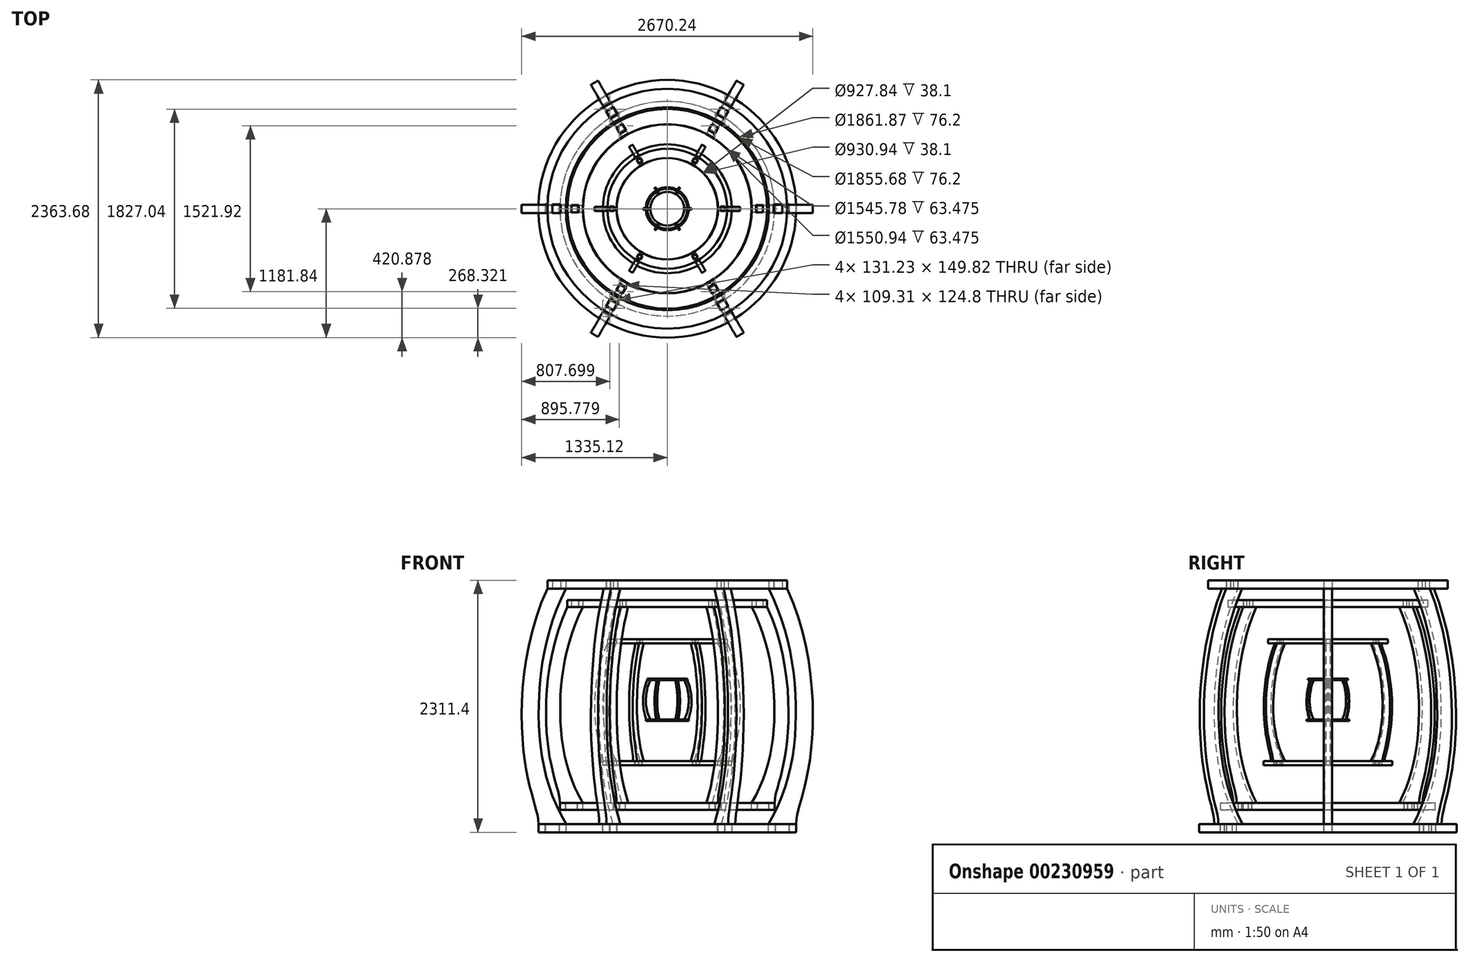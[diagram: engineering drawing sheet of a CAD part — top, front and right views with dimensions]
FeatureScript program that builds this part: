
annotation { "Feature Type Name" : "Feature", "Feature Type Description" : "" }
export const myFeature = defineFeature(function(context is Context, id is Id, definition is map)
    precondition{}
    {
        {
            var Q0;
            Q0=qCreatedBy(makeId("Front.planeOp"),FACE);
            var sketch = newSketch(context, id + "F0", { "sketchPlane" : qUnion([Q0])});
            skLineSegment(sketch, "E0", {"start": v(-1181.84, -1150.9) * mm, "end": v(-927.84, -1150.9) * mm});
            skFitSpline(sketch, "E1", {"points": [v(0, 1953.34) * mm, v(-1100.72, 1005.82) * mm, v(-1321.31, -446.03) * mm, v(-1216.83, -971.67) * mm, v(-1181.84, -1150.9) * mm], "startDerivative": vector(-4000.43, 5.06) * mm, "endDerivative": vector(0, -1489.55) * mm});
            skLineSegment(sketch, "E2", {"start": v(-1099.69, 1008.1) * mm, "end": v(-930.94, 1008.1) * mm});
            skLineSegment(sketch, "E3", {"start": v(-1181.84, -1150.9) * mm, "end": v(-1181.84, -1354.1) * mm});
            skLineSegment(sketch, "E4", {"start": v(-1181.84, -1354.1) * mm, "end": v(-877.04, -1354.1) * mm});
            skLineSegment(sketch, "E5", {"start": v(-877.04, -1354.1) * mm, "end": v(-877.04, -1252.5) * mm});
            skLineSegment(sketch, "E6", {"start": v(-877.04, -1252.5) * mm, "end": v(-927.84, -1252.5) * mm});
            skLineSegment(sketch, "E7", {"start": v(-927.84, -1252.5) * mm, "end": v(-927.84, -1150.9) * mm});
            skFitSpline(sketch, "E8.trimOffspring", {"points": [v(0, -1757.92) * mm, v(-927.84, -1150.9) * mm, v(-1179.31, -127.8) * mm, v(-917.89, 1034.08) * mm, v(0, 1800.66) * mm], "startDerivative": vector(-4973.2, 113.59) * mm, "endDerivative": vector(4756.7, 336.76) * mm});
            skLineSegment(sketch, "E9", {"start": v(-1023.33, 1160.5) * mm, "end": v(-848.12, 1160.5) * mm});
            skLineSegment(sketch, "E10", {"start": v(0, 1953.34) * mm, "end": v(0, 1800.66) * mm});
            skLineSegment(sketch, "E11.bottom", {"start": v(-1118.34, -1074.7) * mm, "end": v(-991.34, -1074.7) * mm});
            skLineSegment(sketch, "E11.top", {"start": v(-1118.34, -1227.1) * mm, "end": v(-991.34, -1227.1) * mm});
            skLineSegment(sketch, "E11.left", {"start": v(-1118.34, -1074.7) * mm, "end": v(-1118.34, -1227.1) * mm});
            skLineSegment(sketch, "E11.right", {"start": v(-991.34, -1074.7) * mm, "end": v(-991.34, -1227.1) * mm});
            skPoint(sketch, "E11.middle", {"position": v(-1054.84, -1150.9) * mm});
            skLineSegment(sketch, "E12.bottom", {"start": v(-1053.41, 1084.3) * mm, "end": v(-977.21, 1084.3) * mm});
            skLineSegment(sketch, "E12.top", {"start": v(-1053.41, 931.9) * mm, "end": v(-977.21, 931.9) * mm});
            skLineSegment(sketch, "E12.left", {"start": v(-1053.41, 1084.3) * mm, "end": v(-1053.41, 931.9) * mm});
            skLineSegment(sketch, "E12.right", {"start": v(-977.21, 1084.3) * mm, "end": v(-977.21, 931.9) * mm});
            skPoint(sketch, "E12.middle", {"position": v(-1015.31, 1008.1) * mm});
            skSolve(sketch);
        }
        {
            var Q0;
            {var subQ5=sQuery(id+"F0.wireOp",EDGE,"E12.bottom");Q0=makeQuery(id+"F0.imprint","IMPRINT",FACE,{"disambiguationData":[TD([[makeQuery(id+"F0.imprint","IMPRINT",EDGE,{"derivedFrom":subQ5}),-1.0]])]});}
            var Q1;
            {var subQ5=sQuery(id+"F0.wireOp",EDGE,"E11.top");Q1=makeQuery(id+"F0.imprint","IMPRINT",FACE,{"disambiguationData":[TD([[makeQuery(id+"F0.imprint","IMPRINT",EDGE,{"derivedFrom":subQ5}),1.0]])]});}
            var Q2;
            {var subQ0=sQuery(id+"F0.wireOp",EDGE,"E11.left");var subQ3=sQuery(id+"F0.wireOp",EDGE,"E0");var subQ4=makeQuery(id+"F0.imprint","INTERSECT",VERTEX,{"derivedFrom":[subQ3,subQ0]});Q2=makeQuery(id+"F0.imprint","IMPRINT",FACE,{"disambiguationData":[TD([[makeQuery(id+"F0.imprint","IMPRINT",EDGE,{"disambiguationData":[TD([[subQ4,-1.0]])],"derivedFrom":subQ3}),1.0]])]});}
            var Q3;
            {var subQ0=sQuery(id+"F0.wireOp",EDGE,"E2");var subQ1=sQuery(id+"F0.wireOp",EDGE,"E1");var subQ2=makeQuery(id+"F0.imprint","INTERSECT",VERTEX,{"derivedFrom":[subQ1,subQ0]});Q3=makeQuery(id+"F0.imprint","IMPRINT",FACE,{"disambiguationData":[TD([[makeQuery(id+"F0.imprint","IMPRINT",EDGE,{"disambiguationData":[TD([[subQ2,-1.0]])],"derivedFrom":subQ0}),-1.0]])]});}
            var Q4;
            {var subQ0=sQuery(id+"F0.wireOp",EDGE,"E8.trimOffspring");var subQ1=sQuery(id+"F0.wireOp",EDGE,"E2");var subQ2=makeQuery(id+"F0.imprint","INTERSECT",VERTEX,{"derivedFrom":[subQ1,subQ0]});Q4=makeQuery(id+"F0.imprint","IMPRINT",FACE,{"disambiguationData":[TD([[makeQuery(id+"F0.imprint","IMPRINT",EDGE,{"disambiguationData":[TD([[subQ2,1.0]])],"derivedFrom":subQ1}),-1.0]])]});}
            var Q5;
            {var subQ0=sQuery(id+"F0.wireOp",EDGE,"E12.left");var subQ5=sQuery(id+"F0.wireOp",EDGE,"E2");var subQ6=makeQuery(id+"F0.imprint","INTERSECT",VERTEX,{"derivedFrom":[subQ5,subQ0]});Q5=makeQuery(id+"F0.imprint","IMPRINT",FACE,{"disambiguationData":[TD([[makeQuery(id+"F0.imprint","IMPRINT",EDGE,{"disambiguationData":[TD([[subQ6,-1.0]])],"derivedFrom":subQ5}),-1.0]])]});}
            extrude(context, id + "F1", {"entities" : qUnion([Q0, Q1, Q2, Q3, Q4, Q5]), "endBound" : BoundingType.SYMMETRIC, "depth" : 76.2 * mm});
        }
        {
            var Q0;
            Q0=makeQuery(id+"F1.opExtrude","SWEPT_BODY",BODY,{"disambiguationData":[OSD([sQuery(id+"F0.wireOp",EDGE,"E0"),sQuery(id+"F0.wireOp",EDGE,"E1"),sQuery(id+"F0.wireOp",EDGE,"E2"),sQuery(id+"F0.wireOp",EDGE,"E8.trimOffspring")])]});
            var Q1;
            Q1=sQuery(id+"F0.wireOp",EDGE,"E10");
            circularPattern(context, id + "F2", {"entities" : qUnion([Q0]), "axis" : qUnion([Q1]), "angle" : 360 * degree, "instanceCount" : 6, "equalSpace" : true});
        }
        {
            var Q0;
            Q0=qCreatedBy(makeId("Top.planeOp"),FACE);
            var Q1;
            Q1=sQuery(id+"F0.wireOp",VERTEX,"E8.trimOffspring.1.internal");
            cPlane(context, id + "F3", {"entities" : qUnion([Q0, Q1]), "cplaneType" : CPlaneType.PLANE_POINT, "offset" : 25.4 * mm, "width" : 152.4 * mm, "height" : 152.4 * mm});
        }
        {
            var Q0;
            Q0=qCreatedBy(id+"F3.planeOp",FACE);
            var sketch = newSketch(context, id + "F4", { "sketchPlane" : qUnion([Q0])});
            skCircle(sketch, "E13", {"center": v(0, 0) * mm, "radius": 1181.84 * mm});
            skCircle(sketch, "E14", {"center": v(0, 0) * mm, "radius": 927.84 * mm});
            skLineSegment(sketch, "E15.bottom", {"start": v(-1118.98, 38.73) * mm, "end": v(-990.7, 38.73) * mm});
            skLineSegment(sketch, "E15.top", {"start": v(-1118.98, -38.74) * mm, "end": v(-990.7, -38.74) * mm});
            skLineSegment(sketch, "E15.left", {"start": v(-1118.98, 38.73) * mm, "end": v(-1118.98, -38.74) * mm});
            skLineSegment(sketch, "E15.right", {"start": v(-990.7, 38.73) * mm, "end": v(-990.7, -38.74) * mm});
            skPoint(sketch, "E15.middle", {"position": v(-1054.84, 0) * mm});
            skLineSegment(sketch, "E16.1.0", {"start": v(-593.03, -949.7) * mm, "end": v(-528.9, -838.6) * mm});
            skLineSegment(sketch, "E16.1.1", {"start": v(-593.03, -949.7) * mm, "end": v(-525.94, -988.43) * mm});
            skLineSegment(sketch, "E16.1.2", {"start": v(-525.94, -988.43) * mm, "end": v(-461.8, -877.34) * mm});
            skLineSegment(sketch, "E16.1.3", {"start": v(-528.9, -838.6) * mm, "end": v(-461.8, -877.34) * mm});
            skLineSegment(sketch, "E16.2.0", {"start": v(525.94, -988.43) * mm, "end": v(461.8, -877.34) * mm});
            skLineSegment(sketch, "E16.2.1", {"start": v(525.94, -988.43) * mm, "end": v(593.03, -949.7) * mm});
            skLineSegment(sketch, "E16.2.2", {"start": v(593.03, -949.7) * mm, "end": v(528.9, -838.6) * mm});
            skLineSegment(sketch, "E16.2.3", {"start": v(461.8, -877.34) * mm, "end": v(528.9, -838.6) * mm});
            skLineSegment(sketch, "E16.3.0", {"start": v(1118.98, -38.74) * mm, "end": v(990.7, -38.74) * mm});
            skLineSegment(sketch, "E16.3.1", {"start": v(1118.98, -38.74) * mm, "end": v(1118.98, 38.73) * mm});
            skLineSegment(sketch, "E16.3.2", {"start": v(1118.98, 38.73) * mm, "end": v(990.7, 38.73) * mm});
            skLineSegment(sketch, "E16.3.3", {"start": v(990.7, -38.74) * mm, "end": v(990.7, 38.73) * mm});
            skLineSegment(sketch, "E16.4.0", {"start": v(593.03, 949.7) * mm, "end": v(528.9, 838.6) * mm});
            skLineSegment(sketch, "E16.4.1", {"start": v(593.03, 949.7) * mm, "end": v(525.94, 988.43) * mm});
            skLineSegment(sketch, "E16.4.2", {"start": v(525.94, 988.43) * mm, "end": v(461.8, 877.34) * mm});
            skLineSegment(sketch, "E16.4.3", {"start": v(528.9, 838.6) * mm, "end": v(461.8, 877.34) * mm});
            skLineSegment(sketch, "E16.5.0", {"start": v(-525.94, 988.43) * mm, "end": v(-461.8, 877.34) * mm});
            skLineSegment(sketch, "E16.5.1", {"start": v(-525.94, 988.43) * mm, "end": v(-593.03, 949.7) * mm});
            skLineSegment(sketch, "E16.5.2", {"start": v(-593.03, 949.7) * mm, "end": v(-528.9, 838.6) * mm});
            skLineSegment(sketch, "E16.5.3", {"start": v(-461.8, 877.34) * mm, "end": v(-528.9, 838.6) * mm});
            skSolve(sketch);
        }
        {
            var Q0;
            Q0=makeQuery(id+"F4.imprint","IMPRINT",FACE,{"disambiguationData":[TD([[makeQuery(id+"F4.imprint","IMPRINT",EDGE,{"derivedFrom":sQuery(id+"F4.wireOp",EDGE,"E13")}),1.0]])]});
            extrude(context, id + "F5", {"entities" : qUnion([Q0]), "oppositeDirection" : true, "depth" : 76.2 * mm});
        }
        {
            var Q0;
            Q0=qCreatedBy(makeId("Top.planeOp"),FACE);
            var Q1;
            Q1=sQuery(id+"F0.wireOp",VERTEX,"E2.end");
            cPlane(context, id + "F6", {"entities" : qUnion([Q0, Q1]), "cplaneType" : CPlaneType.PLANE_POINT, "offset" : 25.4 * mm, "width" : 152.4 * mm, "height" : 152.4 * mm});
        }
        {
            var Q0;
            Q0=qCreatedBy(id+"F6.planeOp",FACE);
            var sketch = newSketch(context, id + "F7", { "sketchPlane" : qUnion([Q0])});
            skCircle(sketch, "E17", {"center": v(0, 0) * mm, "radius": 1099.69 * mm});
            skCircle(sketch, "E18", {"center": v(0, 0) * mm, "radius": 930.94 * mm});
            skLineSegment(sketch, "E19.bottom", {"start": v(-1054.05, 38.74) * mm, "end": v(-976.58, 38.74) * mm});
            skLineSegment(sketch, "E19.top", {"start": v(-1054.05, -38.73) * mm, "end": v(-976.58, -38.73) * mm});
            skLineSegment(sketch, "E19.left", {"start": v(-1054.05, 38.74) * mm, "end": v(-1054.05, -38.73) * mm});
            skLineSegment(sketch, "E19.right", {"start": v(-976.58, 38.74) * mm, "end": v(-976.58, -38.73) * mm});
            skPoint(sketch, "E19.middle", {"position": v(-1015.31, 0) * mm});
            skLineSegment(sketch, "E20.1.0", {"start": v(-560.57, -893.46) * mm, "end": v(-521.83, -826.37) * mm});
            skLineSegment(sketch, "E20.1.1", {"start": v(-560.57, -893.46) * mm, "end": v(-493.48, -932.2) * mm});
            skLineSegment(sketch, "E20.1.2", {"start": v(-493.48, -932.2) * mm, "end": v(-454.74, -865.1) * mm});
            skLineSegment(sketch, "E20.1.3", {"start": v(-521.83, -826.37) * mm, "end": v(-454.74, -865.1) * mm});
            skLineSegment(sketch, "E20.2.0", {"start": v(493.48, -932.2) * mm, "end": v(454.74, -865.1) * mm});
            skLineSegment(sketch, "E20.2.1", {"start": v(493.48, -932.2) * mm, "end": v(560.57, -893.46) * mm});
            skLineSegment(sketch, "E20.2.2", {"start": v(560.57, -893.46) * mm, "end": v(521.83, -826.37) * mm});
            skLineSegment(sketch, "E20.2.3", {"start": v(454.74, -865.1) * mm, "end": v(521.83, -826.37) * mm});
            skLineSegment(sketch, "E20.3.0", {"start": v(1054.05, -38.74) * mm, "end": v(976.58, -38.74) * mm});
            skLineSegment(sketch, "E20.3.1", {"start": v(1054.05, -38.74) * mm, "end": v(1054.05, 38.73) * mm});
            skLineSegment(sketch, "E20.3.2", {"start": v(1054.05, 38.73) * mm, "end": v(976.58, 38.73) * mm});
            skLineSegment(sketch, "E20.3.3", {"start": v(976.58, -38.74) * mm, "end": v(976.58, 38.73) * mm});
            skLineSegment(sketch, "E20.4.0", {"start": v(560.57, 893.46) * mm, "end": v(521.83, 826.37) * mm});
            skLineSegment(sketch, "E20.4.1", {"start": v(560.57, 893.46) * mm, "end": v(493.48, 932.2) * mm});
            skLineSegment(sketch, "E20.4.2", {"start": v(493.48, 932.2) * mm, "end": v(454.74, 865.1) * mm});
            skLineSegment(sketch, "E20.4.3", {"start": v(521.83, 826.37) * mm, "end": v(454.74, 865.1) * mm});
            skLineSegment(sketch, "E20.5.0", {"start": v(-493.48, 932.2) * mm, "end": v(-454.74, 865.1) * mm});
            skLineSegment(sketch, "E20.5.1", {"start": v(-493.48, 932.2) * mm, "end": v(-560.57, 893.46) * mm});
            skLineSegment(sketch, "E20.5.2", {"start": v(-560.57, 893.46) * mm, "end": v(-521.83, 826.37) * mm});
            skLineSegment(sketch, "E20.5.3", {"start": v(-454.74, 865.1) * mm, "end": v(-521.83, 826.37) * mm});
            skSolve(sketch);
        }
        {
            var Q0;
            Q0=makeQuery(id+"F7.imprint","IMPRINT",FACE,{"disambiguationData":[TD([[makeQuery(id+"F7.imprint","IMPRINT",EDGE,{"derivedFrom":sQuery(id+"F7.wireOp",EDGE,"E17")}),1.0]])]});
            extrude(context, id + "F8", {"entities" : qUnion([Q0]), "depth" : 76.2 * mm});
        }
        {
            var Q0;
            Q0=makeQuery(id+"F8.opExtrude","SWEPT_BODY",BODY,{"disambiguationData":[OSD([sQuery(id+"F7.wireOp",EDGE,"E17"),sQuery(id+"F7.wireOp",EDGE,"E18"),sQuery(id+"F7.wireOp",EDGE,"E19.bottom"),sQuery(id+"F7.wireOp",EDGE,"E19.top"),sQuery(id+"F7.wireOp",EDGE,"E19.left"),sQuery(id+"F7.wireOp",EDGE,"E19.right"),sQuery(id+"F7.wireOp",EDGE,"E20.1.0"),sQuery(id+"F7.wireOp",EDGE,"E20.1.1"),sQuery(id+"F7.wireOp",EDGE,"E20.1.2"),sQuery(id+"F7.wireOp",EDGE,"E20.1.3"),sQuery(id+"F7.wireOp",EDGE,"E20.2.0"),sQuery(id+"F7.wireOp",EDGE,"E20.2.1"),sQuery(id+"F7.wireOp",EDGE,"E20.2.2"),sQuery(id+"F7.wireOp",EDGE,"E20.2.3"),sQuery(id+"F7.wireOp",EDGE,"E20.3.0"),sQuery(id+"F7.wireOp",EDGE,"E20.3.1"),sQuery(id+"F7.wireOp",EDGE,"E20.3.2"),sQuery(id+"F7.wireOp",EDGE,"E20.3.3"),sQuery(id+"F7.wireOp",EDGE,"E20.4.0"),sQuery(id+"F7.wireOp",EDGE,"E20.4.1"),sQuery(id+"F7.wireOp",EDGE,"E20.4.2"),sQuery(id+"F7.wireOp",EDGE,"E20.4.3"),sQuery(id+"F7.wireOp",EDGE,"E20.5.0"),sQuery(id+"F7.wireOp",EDGE,"E20.5.1"),sQuery(id+"F7.wireOp",EDGE,"E20.5.2"),sQuery(id+"F7.wireOp",EDGE,"E20.5.3")])]});
            var Q1;
            Q1=makeQuery(id+"F1.opExtrude","SWEPT_BODY",BODY,{"disambiguationData":[OSD([sQuery(id+"F0.wireOp",EDGE,"E0"),sQuery(id+"F0.wireOp",EDGE,"E1"),sQuery(id+"F0.wireOp",EDGE,"E2"),sQuery(id+"F0.wireOp",EDGE,"E8.trimOffspring"),sQuery(id+"F0.wireOp",EDGE,"E11.top"),sQuery(id+"F0.wireOp",EDGE,"E11.left"),sQuery(id+"F0.wireOp",EDGE,"E11.right"),sQuery(id+"F0.wireOp",EDGE,"E12.bottom"),sQuery(id+"F0.wireOp",EDGE,"E12.left"),sQuery(id+"F0.wireOp",EDGE,"E12.right")])]});
            var Q2;
            Q2=makeQuery(id+"F2.opPattern","COPY",BODY,{"derivedFrom":makeQuery(id+"F1.opExtrude","SWEPT_BODY",BODY,{"disambiguationData":[OSD([sQuery(id+"F0.wireOp",EDGE,"E0"),sQuery(id+"F0.wireOp",EDGE,"E1"),sQuery(id+"F0.wireOp",EDGE,"E2"),sQuery(id+"F0.wireOp",EDGE,"E8.trimOffspring"),sQuery(id+"F0.wireOp",EDGE,"E11.top"),sQuery(id+"F0.wireOp",EDGE,"E11.left"),sQuery(id+"F0.wireOp",EDGE,"E11.right"),sQuery(id+"F0.wireOp",EDGE,"E12.bottom"),sQuery(id+"F0.wireOp",EDGE,"E12.left"),sQuery(id+"F0.wireOp",EDGE,"E12.right")])]}),"instanceName":"5"});
            var Q3;
            Q3=makeQuery(id+"F2.opPattern","COPY",BODY,{"derivedFrom":makeQuery(id+"F1.opExtrude","SWEPT_BODY",BODY,{"disambiguationData":[OSD([sQuery(id+"F0.wireOp",EDGE,"E0"),sQuery(id+"F0.wireOp",EDGE,"E1"),sQuery(id+"F0.wireOp",EDGE,"E2"),sQuery(id+"F0.wireOp",EDGE,"E8.trimOffspring"),sQuery(id+"F0.wireOp",EDGE,"E11.top"),sQuery(id+"F0.wireOp",EDGE,"E11.left"),sQuery(id+"F0.wireOp",EDGE,"E11.right"),sQuery(id+"F0.wireOp",EDGE,"E12.bottom"),sQuery(id+"F0.wireOp",EDGE,"E12.left"),sQuery(id+"F0.wireOp",EDGE,"E12.right")])]}),"instanceName":"1"});
            var Q4;
            Q4=makeQuery(id+"F2.opPattern","COPY",BODY,{"derivedFrom":makeQuery(id+"F1.opExtrude","SWEPT_BODY",BODY,{"disambiguationData":[OSD([sQuery(id+"F0.wireOp",EDGE,"E0"),sQuery(id+"F0.wireOp",EDGE,"E1"),sQuery(id+"F0.wireOp",EDGE,"E2"),sQuery(id+"F0.wireOp",EDGE,"E8.trimOffspring"),sQuery(id+"F0.wireOp",EDGE,"E11.top"),sQuery(id+"F0.wireOp",EDGE,"E11.left"),sQuery(id+"F0.wireOp",EDGE,"E11.right"),sQuery(id+"F0.wireOp",EDGE,"E12.bottom"),sQuery(id+"F0.wireOp",EDGE,"E12.left"),sQuery(id+"F0.wireOp",EDGE,"E12.right")])]}),"instanceName":"2"});
            var Q5;
            Q5=makeQuery(id+"F2.opPattern","COPY",BODY,{"derivedFrom":makeQuery(id+"F1.opExtrude","SWEPT_BODY",BODY,{"disambiguationData":[OSD([sQuery(id+"F0.wireOp",EDGE,"E0"),sQuery(id+"F0.wireOp",EDGE,"E1"),sQuery(id+"F0.wireOp",EDGE,"E2"),sQuery(id+"F0.wireOp",EDGE,"E8.trimOffspring"),sQuery(id+"F0.wireOp",EDGE,"E11.top"),sQuery(id+"F0.wireOp",EDGE,"E11.left"),sQuery(id+"F0.wireOp",EDGE,"E11.right"),sQuery(id+"F0.wireOp",EDGE,"E12.bottom"),sQuery(id+"F0.wireOp",EDGE,"E12.left"),sQuery(id+"F0.wireOp",EDGE,"E12.right")])]}),"instanceName":"3"});
            var Q6;
            Q6=makeQuery(id+"F2.opPattern","COPY",BODY,{"derivedFrom":makeQuery(id+"F1.opExtrude","SWEPT_BODY",BODY,{"disambiguationData":[OSD([sQuery(id+"F0.wireOp",EDGE,"E0"),sQuery(id+"F0.wireOp",EDGE,"E1"),sQuery(id+"F0.wireOp",EDGE,"E2"),sQuery(id+"F0.wireOp",EDGE,"E8.trimOffspring"),sQuery(id+"F0.wireOp",EDGE,"E11.top"),sQuery(id+"F0.wireOp",EDGE,"E11.left"),sQuery(id+"F0.wireOp",EDGE,"E11.right"),sQuery(id+"F0.wireOp",EDGE,"E12.bottom"),sQuery(id+"F0.wireOp",EDGE,"E12.left"),sQuery(id+"F0.wireOp",EDGE,"E12.right")])]}),"instanceName":"4"});
            var Q7;
            Q7=makeQuery(id+"F5.opExtrude","SWEPT_BODY",BODY,{"disambiguationData":[OSD([sQuery(id+"F4.wireOp",EDGE,"E13"),sQuery(id+"F4.wireOp",EDGE,"E14"),sQuery(id+"F4.wireOp",EDGE,"E15.bottom"),sQuery(id+"F4.wireOp",EDGE,"E15.top"),sQuery(id+"F4.wireOp",EDGE,"E15.left"),sQuery(id+"F4.wireOp",EDGE,"E15.right"),sQuery(id+"F4.wireOp",EDGE,"E16.1.0"),sQuery(id+"F4.wireOp",EDGE,"E16.1.1"),sQuery(id+"F4.wireOp",EDGE,"E16.1.2"),sQuery(id+"F4.wireOp",EDGE,"E16.1.3"),sQuery(id+"F4.wireOp",EDGE,"E16.2.0"),sQuery(id+"F4.wireOp",EDGE,"E16.2.1"),sQuery(id+"F4.wireOp",EDGE,"E16.2.2"),sQuery(id+"F4.wireOp",EDGE,"E16.2.3"),sQuery(id+"F4.wireOp",EDGE,"E16.3.0"),sQuery(id+"F4.wireOp",EDGE,"E16.3.1"),sQuery(id+"F4.wireOp",EDGE,"E16.3.2"),sQuery(id+"F4.wireOp",EDGE,"E16.3.3"),sQuery(id+"F4.wireOp",EDGE,"E16.4.0"),sQuery(id+"F4.wireOp",EDGE,"E16.4.1"),sQuery(id+"F4.wireOp",EDGE,"E16.4.2"),sQuery(id+"F4.wireOp",EDGE,"E16.4.3"),sQuery(id+"F4.wireOp",EDGE,"E16.5.0"),sQuery(id+"F4.wireOp",EDGE,"E16.5.1"),sQuery(id+"F4.wireOp",EDGE,"E16.5.2"),sQuery(id+"F4.wireOp",EDGE,"E16.5.3")])]});
            var Q8;
            Q8=qCreatedBy(makeId("Origin.pointOp"),VERTEX);
            transform(context, id + "F9", {"entities" : qUnion([Q0, Q1, Q2, Q3, Q4, Q5, Q6, Q7]), "transformType" : TransformType.SCALE_UNIFORMLY, "scale" : .1666, "scalePoint" : qUnion([Q8]), "makeCopy" : true});
        }
        {
            var Q0;
            Q0=makeQuery(id+"F8.opExtrude","SWEPT_BODY",BODY,{"disambiguationData":[OSD([sQuery(id+"F7.wireOp",EDGE,"E17"),sQuery(id+"F7.wireOp",EDGE,"E18"),sQuery(id+"F7.wireOp",EDGE,"E19.bottom"),sQuery(id+"F7.wireOp",EDGE,"E19.top"),sQuery(id+"F7.wireOp",EDGE,"E19.left"),sQuery(id+"F7.wireOp",EDGE,"E19.right"),sQuery(id+"F7.wireOp",EDGE,"E20.1.0"),sQuery(id+"F7.wireOp",EDGE,"E20.1.1"),sQuery(id+"F7.wireOp",EDGE,"E20.1.2"),sQuery(id+"F7.wireOp",EDGE,"E20.1.3"),sQuery(id+"F7.wireOp",EDGE,"E20.2.0"),sQuery(id+"F7.wireOp",EDGE,"E20.2.1"),sQuery(id+"F7.wireOp",EDGE,"E20.2.2"),sQuery(id+"F7.wireOp",EDGE,"E20.2.3"),sQuery(id+"F7.wireOp",EDGE,"E20.3.0"),sQuery(id+"F7.wireOp",EDGE,"E20.3.1"),sQuery(id+"F7.wireOp",EDGE,"E20.3.2"),sQuery(id+"F7.wireOp",EDGE,"E20.3.3"),sQuery(id+"F7.wireOp",EDGE,"E20.4.0"),sQuery(id+"F7.wireOp",EDGE,"E20.4.1"),sQuery(id+"F7.wireOp",EDGE,"E20.4.2"),sQuery(id+"F7.wireOp",EDGE,"E20.4.3"),sQuery(id+"F7.wireOp",EDGE,"E20.5.0"),sQuery(id+"F7.wireOp",EDGE,"E20.5.1"),sQuery(id+"F7.wireOp",EDGE,"E20.5.2"),sQuery(id+"F7.wireOp",EDGE,"E20.5.3")])]});
            var Q1;
            Q1=makeQuery(id+"F1.opExtrude","SWEPT_BODY",BODY,{"disambiguationData":[OSD([sQuery(id+"F0.wireOp",EDGE,"E0"),sQuery(id+"F0.wireOp",EDGE,"E1"),sQuery(id+"F0.wireOp",EDGE,"E2"),sQuery(id+"F0.wireOp",EDGE,"E8.trimOffspring"),sQuery(id+"F0.wireOp",EDGE,"E11.top"),sQuery(id+"F0.wireOp",EDGE,"E11.left"),sQuery(id+"F0.wireOp",EDGE,"E11.right"),sQuery(id+"F0.wireOp",EDGE,"E12.bottom"),sQuery(id+"F0.wireOp",EDGE,"E12.left"),sQuery(id+"F0.wireOp",EDGE,"E12.right")])]});
            var Q2;
            Q2=makeQuery(id+"F2.opPattern","COPY",BODY,{"derivedFrom":makeQuery(id+"F1.opExtrude","SWEPT_BODY",BODY,{"disambiguationData":[OSD([sQuery(id+"F0.wireOp",EDGE,"E0"),sQuery(id+"F0.wireOp",EDGE,"E1"),sQuery(id+"F0.wireOp",EDGE,"E2"),sQuery(id+"F0.wireOp",EDGE,"E8.trimOffspring"),sQuery(id+"F0.wireOp",EDGE,"E11.top"),sQuery(id+"F0.wireOp",EDGE,"E11.left"),sQuery(id+"F0.wireOp",EDGE,"E11.right"),sQuery(id+"F0.wireOp",EDGE,"E12.bottom"),sQuery(id+"F0.wireOp",EDGE,"E12.left"),sQuery(id+"F0.wireOp",EDGE,"E12.right")])]}),"instanceName":"1"});
            var Q3;
            Q3=makeQuery(id+"F2.opPattern","COPY",BODY,{"derivedFrom":makeQuery(id+"F1.opExtrude","SWEPT_BODY",BODY,{"disambiguationData":[OSD([sQuery(id+"F0.wireOp",EDGE,"E0"),sQuery(id+"F0.wireOp",EDGE,"E1"),sQuery(id+"F0.wireOp",EDGE,"E2"),sQuery(id+"F0.wireOp",EDGE,"E8.trimOffspring"),sQuery(id+"F0.wireOp",EDGE,"E11.top"),sQuery(id+"F0.wireOp",EDGE,"E11.left"),sQuery(id+"F0.wireOp",EDGE,"E11.right"),sQuery(id+"F0.wireOp",EDGE,"E12.bottom"),sQuery(id+"F0.wireOp",EDGE,"E12.left"),sQuery(id+"F0.wireOp",EDGE,"E12.right")])]}),"instanceName":"2"});
            var Q4;
            Q4=makeQuery(id+"F2.opPattern","COPY",BODY,{"derivedFrom":makeQuery(id+"F1.opExtrude","SWEPT_BODY",BODY,{"disambiguationData":[OSD([sQuery(id+"F0.wireOp",EDGE,"E0"),sQuery(id+"F0.wireOp",EDGE,"E1"),sQuery(id+"F0.wireOp",EDGE,"E2"),sQuery(id+"F0.wireOp",EDGE,"E8.trimOffspring"),sQuery(id+"F0.wireOp",EDGE,"E11.top"),sQuery(id+"F0.wireOp",EDGE,"E11.left"),sQuery(id+"F0.wireOp",EDGE,"E11.right"),sQuery(id+"F0.wireOp",EDGE,"E12.bottom"),sQuery(id+"F0.wireOp",EDGE,"E12.left"),sQuery(id+"F0.wireOp",EDGE,"E12.right")])]}),"instanceName":"3"});
            var Q5;
            Q5=makeQuery(id+"F2.opPattern","COPY",BODY,{"derivedFrom":makeQuery(id+"F1.opExtrude","SWEPT_BODY",BODY,{"disambiguationData":[OSD([sQuery(id+"F0.wireOp",EDGE,"E0"),sQuery(id+"F0.wireOp",EDGE,"E1"),sQuery(id+"F0.wireOp",EDGE,"E2"),sQuery(id+"F0.wireOp",EDGE,"E8.trimOffspring"),sQuery(id+"F0.wireOp",EDGE,"E11.top"),sQuery(id+"F0.wireOp",EDGE,"E11.left"),sQuery(id+"F0.wireOp",EDGE,"E11.right"),sQuery(id+"F0.wireOp",EDGE,"E12.bottom"),sQuery(id+"F0.wireOp",EDGE,"E12.left"),sQuery(id+"F0.wireOp",EDGE,"E12.right")])]}),"instanceName":"4"});
            var Q6;
            Q6=makeQuery(id+"F5.opExtrude","SWEPT_BODY",BODY,{"disambiguationData":[OSD([sQuery(id+"F4.wireOp",EDGE,"E13"),sQuery(id+"F4.wireOp",EDGE,"E14"),sQuery(id+"F4.wireOp",EDGE,"E15.bottom"),sQuery(id+"F4.wireOp",EDGE,"E15.top"),sQuery(id+"F4.wireOp",EDGE,"E15.left"),sQuery(id+"F4.wireOp",EDGE,"E15.right"),sQuery(id+"F4.wireOp",EDGE,"E16.1.0"),sQuery(id+"F4.wireOp",EDGE,"E16.1.1"),sQuery(id+"F4.wireOp",EDGE,"E16.1.2"),sQuery(id+"F4.wireOp",EDGE,"E16.1.3"),sQuery(id+"F4.wireOp",EDGE,"E16.2.0"),sQuery(id+"F4.wireOp",EDGE,"E16.2.1"),sQuery(id+"F4.wireOp",EDGE,"E16.2.2"),sQuery(id+"F4.wireOp",EDGE,"E16.2.3"),sQuery(id+"F4.wireOp",EDGE,"E16.3.0"),sQuery(id+"F4.wireOp",EDGE,"E16.3.1"),sQuery(id+"F4.wireOp",EDGE,"E16.3.2"),sQuery(id+"F4.wireOp",EDGE,"E16.3.3"),sQuery(id+"F4.wireOp",EDGE,"E16.4.0"),sQuery(id+"F4.wireOp",EDGE,"E16.4.1"),sQuery(id+"F4.wireOp",EDGE,"E16.4.2"),sQuery(id+"F4.wireOp",EDGE,"E16.4.3"),sQuery(id+"F4.wireOp",EDGE,"E16.5.0"),sQuery(id+"F4.wireOp",EDGE,"E16.5.1"),sQuery(id+"F4.wireOp",EDGE,"E16.5.2"),sQuery(id+"F4.wireOp",EDGE,"E16.5.3")])]});
            var Q7;
            Q7=makeQuery(id+"F2.opPattern","COPY",BODY,{"derivedFrom":makeQuery(id+"F1.opExtrude","SWEPT_BODY",BODY,{"disambiguationData":[OSD([sQuery(id+"F0.wireOp",EDGE,"E0"),sQuery(id+"F0.wireOp",EDGE,"E1"),sQuery(id+"F0.wireOp",EDGE,"E2"),sQuery(id+"F0.wireOp",EDGE,"E8.trimOffspring"),sQuery(id+"F0.wireOp",EDGE,"E11.top"),sQuery(id+"F0.wireOp",EDGE,"E11.left"),sQuery(id+"F0.wireOp",EDGE,"E11.right"),sQuery(id+"F0.wireOp",EDGE,"E12.bottom"),sQuery(id+"F0.wireOp",EDGE,"E12.left"),sQuery(id+"F0.wireOp",EDGE,"E12.right")])]}),"instanceName":"5"});
            var Q8;
            Q8=qCreatedBy(makeId("Origin.pointOp"),VERTEX);
            transform(context, id + "F10", {"entities" : qUnion([Q0, Q1, Q2, Q3, Q4, Q5, Q6, Q7]), "transformType" : TransformType.SCALE_UNIFORMLY, "scale" : .833, "scalePoint" : qUnion([Q8]), "makeCopy" : true});
        }
        {
            var Q0;
            Q0=makeQuery(id+"F8.opExtrude","SWEPT_BODY",BODY,{"disambiguationData":[OSD([sQuery(id+"F7.wireOp",EDGE,"E17"),sQuery(id+"F7.wireOp",EDGE,"E18"),sQuery(id+"F7.wireOp",EDGE,"E19.bottom"),sQuery(id+"F7.wireOp",EDGE,"E19.top"),sQuery(id+"F7.wireOp",EDGE,"E19.left"),sQuery(id+"F7.wireOp",EDGE,"E19.right"),sQuery(id+"F7.wireOp",EDGE,"E20.1.0"),sQuery(id+"F7.wireOp",EDGE,"E20.1.1"),sQuery(id+"F7.wireOp",EDGE,"E20.1.2"),sQuery(id+"F7.wireOp",EDGE,"E20.1.3"),sQuery(id+"F7.wireOp",EDGE,"E20.2.0"),sQuery(id+"F7.wireOp",EDGE,"E20.2.1"),sQuery(id+"F7.wireOp",EDGE,"E20.2.2"),sQuery(id+"F7.wireOp",EDGE,"E20.2.3"),sQuery(id+"F7.wireOp",EDGE,"E20.3.0"),sQuery(id+"F7.wireOp",EDGE,"E20.3.1"),sQuery(id+"F7.wireOp",EDGE,"E20.3.2"),sQuery(id+"F7.wireOp",EDGE,"E20.3.3"),sQuery(id+"F7.wireOp",EDGE,"E20.4.0"),sQuery(id+"F7.wireOp",EDGE,"E20.4.1"),sQuery(id+"F7.wireOp",EDGE,"E20.4.2"),sQuery(id+"F7.wireOp",EDGE,"E20.4.3"),sQuery(id+"F7.wireOp",EDGE,"E20.5.0"),sQuery(id+"F7.wireOp",EDGE,"E20.5.1"),sQuery(id+"F7.wireOp",EDGE,"E20.5.2"),sQuery(id+"F7.wireOp",EDGE,"E20.5.3")])]});
            var Q1;
            Q1=makeQuery(id+"F2.opPattern","COPY",BODY,{"derivedFrom":makeQuery(id+"F1.opExtrude","SWEPT_BODY",BODY,{"disambiguationData":[OSD([sQuery(id+"F0.wireOp",EDGE,"E0"),sQuery(id+"F0.wireOp",EDGE,"E1"),sQuery(id+"F0.wireOp",EDGE,"E2"),sQuery(id+"F0.wireOp",EDGE,"E8.trimOffspring"),sQuery(id+"F0.wireOp",EDGE,"E11.top"),sQuery(id+"F0.wireOp",EDGE,"E11.left"),sQuery(id+"F0.wireOp",EDGE,"E11.right"),sQuery(id+"F0.wireOp",EDGE,"E12.bottom"),sQuery(id+"F0.wireOp",EDGE,"E12.left"),sQuery(id+"F0.wireOp",EDGE,"E12.right")])]}),"instanceName":"5"});
            var Q2;
            Q2=makeQuery(id+"F1.opExtrude","SWEPT_BODY",BODY,{"disambiguationData":[OSD([sQuery(id+"F0.wireOp",EDGE,"E0"),sQuery(id+"F0.wireOp",EDGE,"E1"),sQuery(id+"F0.wireOp",EDGE,"E2"),sQuery(id+"F0.wireOp",EDGE,"E8.trimOffspring"),sQuery(id+"F0.wireOp",EDGE,"E11.top"),sQuery(id+"F0.wireOp",EDGE,"E11.left"),sQuery(id+"F0.wireOp",EDGE,"E11.right"),sQuery(id+"F0.wireOp",EDGE,"E12.bottom"),sQuery(id+"F0.wireOp",EDGE,"E12.left"),sQuery(id+"F0.wireOp",EDGE,"E12.right")])]});
            var Q3;
            Q3=makeQuery(id+"F2.opPattern","COPY",BODY,{"derivedFrom":makeQuery(id+"F1.opExtrude","SWEPT_BODY",BODY,{"disambiguationData":[OSD([sQuery(id+"F0.wireOp",EDGE,"E0"),sQuery(id+"F0.wireOp",EDGE,"E1"),sQuery(id+"F0.wireOp",EDGE,"E2"),sQuery(id+"F0.wireOp",EDGE,"E8.trimOffspring"),sQuery(id+"F0.wireOp",EDGE,"E11.top"),sQuery(id+"F0.wireOp",EDGE,"E11.left"),sQuery(id+"F0.wireOp",EDGE,"E11.right"),sQuery(id+"F0.wireOp",EDGE,"E12.bottom"),sQuery(id+"F0.wireOp",EDGE,"E12.left"),sQuery(id+"F0.wireOp",EDGE,"E12.right")])]}),"instanceName":"4"});
            var Q4;
            Q4=makeQuery(id+"F2.opPattern","COPY",BODY,{"derivedFrom":makeQuery(id+"F1.opExtrude","SWEPT_BODY",BODY,{"disambiguationData":[OSD([sQuery(id+"F0.wireOp",EDGE,"E0"),sQuery(id+"F0.wireOp",EDGE,"E1"),sQuery(id+"F0.wireOp",EDGE,"E2"),sQuery(id+"F0.wireOp",EDGE,"E8.trimOffspring"),sQuery(id+"F0.wireOp",EDGE,"E11.top"),sQuery(id+"F0.wireOp",EDGE,"E11.left"),sQuery(id+"F0.wireOp",EDGE,"E11.right"),sQuery(id+"F0.wireOp",EDGE,"E12.bottom"),sQuery(id+"F0.wireOp",EDGE,"E12.left"),sQuery(id+"F0.wireOp",EDGE,"E12.right")])]}),"instanceName":"3"});
            var Q5;
            Q5=makeQuery(id+"F2.opPattern","COPY",BODY,{"derivedFrom":makeQuery(id+"F1.opExtrude","SWEPT_BODY",BODY,{"disambiguationData":[OSD([sQuery(id+"F0.wireOp",EDGE,"E0"),sQuery(id+"F0.wireOp",EDGE,"E1"),sQuery(id+"F0.wireOp",EDGE,"E2"),sQuery(id+"F0.wireOp",EDGE,"E8.trimOffspring"),sQuery(id+"F0.wireOp",EDGE,"E11.top"),sQuery(id+"F0.wireOp",EDGE,"E11.left"),sQuery(id+"F0.wireOp",EDGE,"E11.right"),sQuery(id+"F0.wireOp",EDGE,"E12.bottom"),sQuery(id+"F0.wireOp",EDGE,"E12.left"),sQuery(id+"F0.wireOp",EDGE,"E12.right")])]}),"instanceName":"1"});
            var Q6;
            Q6=makeQuery(id+"F2.opPattern","COPY",BODY,{"derivedFrom":makeQuery(id+"F1.opExtrude","SWEPT_BODY",BODY,{"disambiguationData":[OSD([sQuery(id+"F0.wireOp",EDGE,"E0"),sQuery(id+"F0.wireOp",EDGE,"E1"),sQuery(id+"F0.wireOp",EDGE,"E2"),sQuery(id+"F0.wireOp",EDGE,"E8.trimOffspring"),sQuery(id+"F0.wireOp",EDGE,"E11.top"),sQuery(id+"F0.wireOp",EDGE,"E11.left"),sQuery(id+"F0.wireOp",EDGE,"E11.right"),sQuery(id+"F0.wireOp",EDGE,"E12.bottom"),sQuery(id+"F0.wireOp",EDGE,"E12.left"),sQuery(id+"F0.wireOp",EDGE,"E12.right")])]}),"instanceName":"2"});
            var Q7;
            Q7=makeQuery(id+"F5.opExtrude","SWEPT_BODY",BODY,{"disambiguationData":[OSD([sQuery(id+"F4.wireOp",EDGE,"E13"),sQuery(id+"F4.wireOp",EDGE,"E14"),sQuery(id+"F4.wireOp",EDGE,"E15.bottom"),sQuery(id+"F4.wireOp",EDGE,"E15.top"),sQuery(id+"F4.wireOp",EDGE,"E15.left"),sQuery(id+"F4.wireOp",EDGE,"E15.right"),sQuery(id+"F4.wireOp",EDGE,"E16.1.0"),sQuery(id+"F4.wireOp",EDGE,"E16.1.1"),sQuery(id+"F4.wireOp",EDGE,"E16.1.2"),sQuery(id+"F4.wireOp",EDGE,"E16.1.3"),sQuery(id+"F4.wireOp",EDGE,"E16.2.0"),sQuery(id+"F4.wireOp",EDGE,"E16.2.1"),sQuery(id+"F4.wireOp",EDGE,"E16.2.2"),sQuery(id+"F4.wireOp",EDGE,"E16.2.3"),sQuery(id+"F4.wireOp",EDGE,"E16.3.0"),sQuery(id+"F4.wireOp",EDGE,"E16.3.1"),sQuery(id+"F4.wireOp",EDGE,"E16.3.2"),sQuery(id+"F4.wireOp",EDGE,"E16.3.3"),sQuery(id+"F4.wireOp",EDGE,"E16.4.0"),sQuery(id+"F4.wireOp",EDGE,"E16.4.1"),sQuery(id+"F4.wireOp",EDGE,"E16.4.2"),sQuery(id+"F4.wireOp",EDGE,"E16.4.3"),sQuery(id+"F4.wireOp",EDGE,"E16.5.0"),sQuery(id+"F4.wireOp",EDGE,"E16.5.1"),sQuery(id+"F4.wireOp",EDGE,"E16.5.2"),sQuery(id+"F4.wireOp",EDGE,"E16.5.3")])]});
            var Q8;
            Q8=qCreatedBy(makeId("Origin.pointOp"),VERTEX);
            transform(context, id + "F11", {"entities" : qUnion([Q0, Q1, Q2, Q3, Q4, Q5, Q6, Q7]), "transformType" : TransformType.SCALE_UNIFORMLY, "scale" : .5, "scalePoint" : qUnion([Q8]), "makeCopy" : true});
        }
    });
